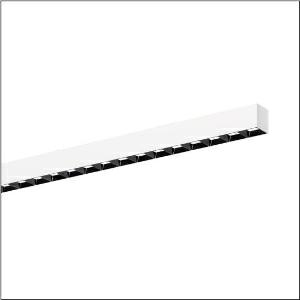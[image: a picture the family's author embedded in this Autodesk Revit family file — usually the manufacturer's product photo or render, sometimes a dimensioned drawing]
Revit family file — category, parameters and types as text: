
# Revit family: silica_21_51mx24dc4awb
name_source: partatom
category: Lighting Fixtures
units: mm (PartAtom-declared; Revit-internal decimal feet)

## family parameters
Cut with Voids When Loaded = No
Host = Face
Light Source = No
Part Type = Normal
Room Calculation Point = No
Round Connector Dimension = Use Diameter
Shared = No

## types (1)
- --- (1 x LED, 10800 lm, 73.7 W, 4000K)
    Apparent Load = 74 VA
    CIE Flux Codes = 74 94 99 100 100
    Color Rendering = 80
    Color Temperature = 4000K
    Default Elevation = 1800 mm
    Description = Silica 21, office luminaire, primary light control with darklight reflector, of PMMA, black, CAT 2 (L<= 3000cd/m²), light emission: direct distribution, primary light characteristic: asymmetric, installation type: surface-mounted, LED, rated luminous flux: 10.800lm, luminous efficacy: 147lm/W, light colour: 840, colour temperature: 4000K, control gear: DALI 2, with terminal, 3+2-pole, max. 2.5mm², mains connection: 220..240V, AC, 50/60Hz, rated input power: 73.7W, luminaire housing, of aluminium, traffic white (RAL 9016), length: 3.004mm, width: 53mm, height: 53mm, protection rating (complete): IP20, insulation class (complete): insulation class I (protective earthing), certification: CE, permissible operating ambient temperature: 0..+35°C, standard: EN 50419, packaging unit: 1 piece
    Height = 53 mm
    Lamp = 1 x LED
    Lamp Light Flux = 10800 lm
    Lamp Power = 73.7 W
    Lamp count = 1
    Length = 3004 mm
    Luminous efficacy = 147 lm/W
    Manufacturer = Siteco
    ModVariant = No
    Model = 51MX24DC4AWB
    Mounting Place = Ceiling
    Mounting Type = Surface mounted
    Number of Poles = 1
    OnlyDefault = Yes
    Power Factor = 1
    Product Name = Silica 21
    Product group = office luminaire | ceiling mounted
    ProductGroupID = 301
    Protection Class = Protection class I
    Protection Degree = IP 20
    RLX_Detail_Level = 1
    RLX_Emergency_Light_Flux = 0 lm
    RLX_Emergency_Type = 0
    RLX_Emergency_Type_DB = No
    RlxData = <blob elided: 62201 chars, md5=dae445ad>
    Socket = socket
    Standby Power = 0 W
    System Light Flux = 10800 lm
    System Power = 74 W
    Type Comments = factory setting: luminous flux: 100 % | dim-lin: 254 | 418 mA
    Type Image = l_1335873.jpg
    URL = http://relux.com
    VarID = @adj_124841
    Voltage = 0 V
    Weight = 0.00 kg
    Width = 53 mm

## geometry (parser evidence)
native form markers: Blend x4, Sweep x13
no freeform markers — native parametric forms only
